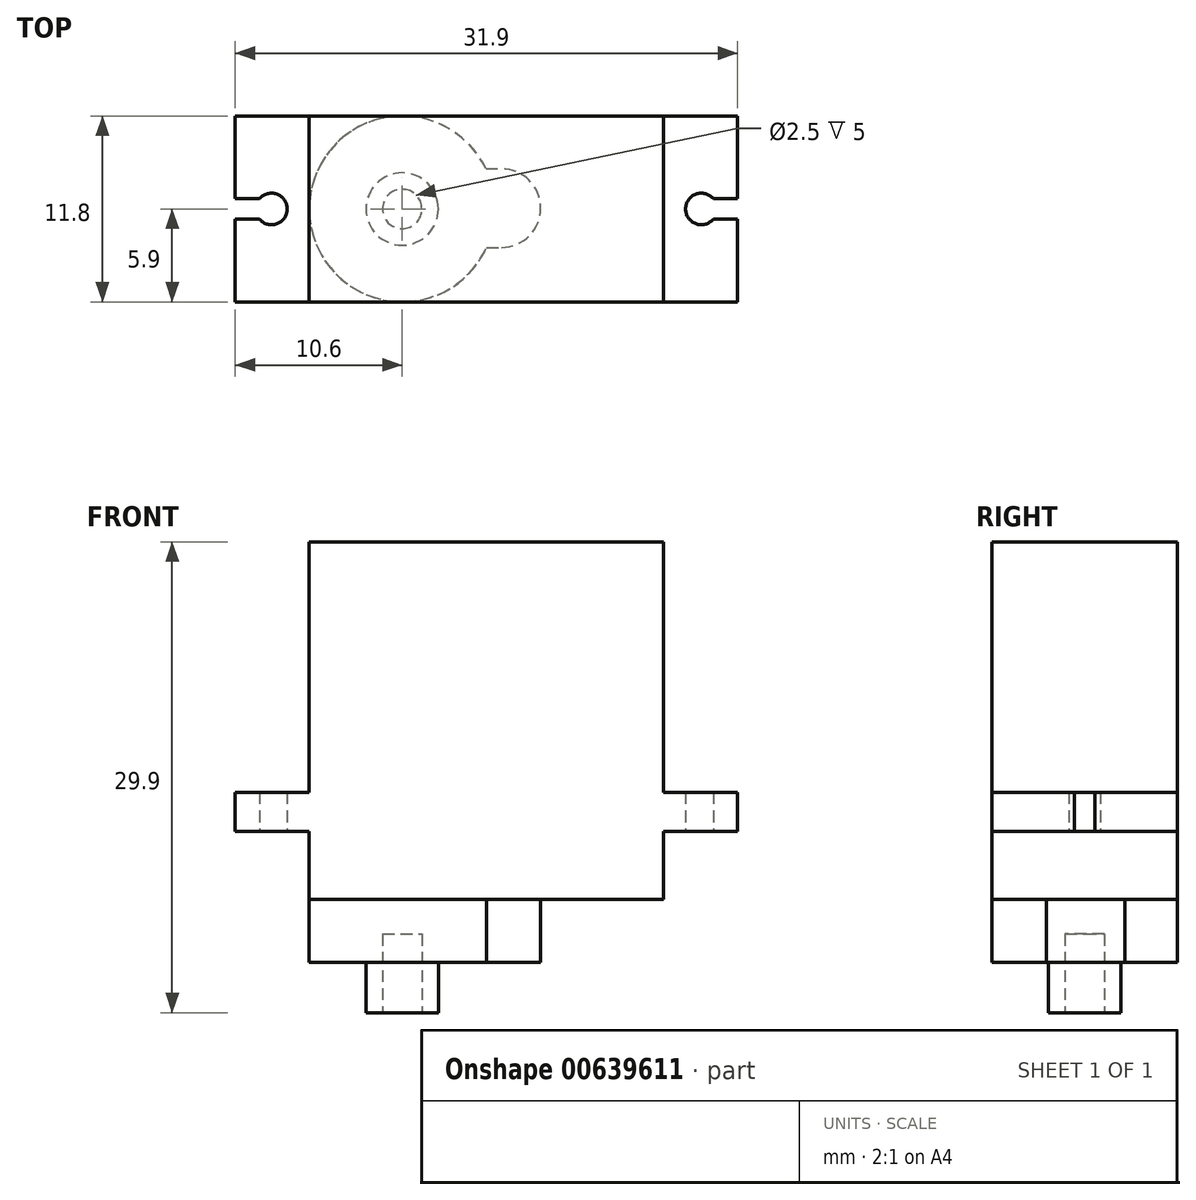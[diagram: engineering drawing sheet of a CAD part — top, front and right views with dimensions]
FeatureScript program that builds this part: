
annotation { "Feature Type Name" : "Feature", "Feature Type Description" : "" }
export const myFeature = defineFeature(function(context is Context, id is Id, definition is map)
    precondition{}
    {
        {
            var Q0;
            Q0=qCreatedBy(makeId("Top.planeOp"),FACE);
            var sketch = newSketch(context, id + "F0", { "sketchPlane" : qUnion([Q0])});
            skLineSegment(sketch, "E0.bottom", {"start": v(0, 0) * mm, "end": v(15.95, 0) * mm});
            skLineSegment(sketch, "E0.top", {"start": v(0, 11.8) * mm, "end": v(15.95, 11.8) * mm});
            skLineSegment(sketch, "E0.left", {"start": v(0, 0) * mm, "end": v(0, 11.8) * mm});
            skLineSegment(sketch, "E0.right", {"start": v(15.95, 0) * mm, "end": v(15.95, 11.8) * mm});
            skSolve(sketch);
        }
        {
            var Q0;
            Q0=makeQuery(id+"F0.imprint","IMPRINT",FACE,{"disambiguationData":[TD([[makeQuery(id+"F0.imprint","IMPRINT",EDGE,{"derivedFrom":sQuery(id+"F0.wireOp",EDGE,"E0.bottom")}),1.0]])]});
            var sketch = newSketch(context, id + "F1", { "sketchPlane" : qUnion([Q0])});
            skArc(sketch, "E1", {"start": v(1.54, 5.25) * mm, "mid": v(3.3, 5.9) * mm, "end": v(1.54, 6.55) * mm});
            skLineSegment(sketch, "E2", {"start": v(0, 5.25) * mm, "end": v(1.54, 5.25) * mm});
            skLineSegment(sketch, "E3", {"start": v(0, 6.55) * mm, "end": v(1.54, 6.55) * mm});
            skSolve(sketch);
        }
        {
            var Q0;
            Q0=makeQuery(id+"F1.imprint","IMPRINT",FACE,{"disambiguationData":[TD([[makeQuery(id+"F1.imprint","IMPRINT",EDGE,{"derivedFrom":sQuery(id+"F1.wireOp",EDGE,"E1")}),-1.0]])]});
            extrude(context, id + "F2", {"entities" : qUnion([Q0]), "depth" : 22.7 * mm, "offsetDistance" : 25 * mm});
        }
        {
            var Q0;
            Q0=makeQuery(id+"F2.opExtrude","SWEPT_FACE",FACE,{"disambiguationData":[OSD([sQuery(id+"F0.wireOp",EDGE,"E0.top")])]});
            var sketch = newSketch(context, id + "F3", { "sketchPlane" : qUnion([Q0])});
            skLineSegment(sketch, "E4", {"start": v(-4.7, 0) * mm, "end": v(-4.7, 4.3) * mm});
            skLineSegment(sketch, "E5", {"start": v(-4.7, 4.3) * mm, "end": v(0, 4.3) * mm});
            skLineSegment(sketch, "E6", {"start": v(0, 6.8) * mm, "end": v(-4.7, 6.8) * mm});
            skLineSegment(sketch, "E7", {"start": v(-4.7, 6.8) * mm, "end": v(-4.7, 22.7) * mm});
            skSolve(sketch);
        }
        {
            var Q0;
            {var subQ0=sQuery(id+"F3.wireOp",EDGE,"E4");Q0=makeQuery(id+"F3.imprint","IMPRINT",FACE,{"disambiguationData":[TD([[makeQuery(id+"F3.imprint","IMPRINT",EDGE,{"derivedFrom":subQ0}),-1.0]])]});}
            var Q1;
            {var subQ0=sQuery(id+"F3.wireOp",EDGE,"E6");Q1=makeQuery(id+"F3.imprint","IMPRINT",FACE,{"disambiguationData":[TD([[makeQuery(id+"F3.imprint","IMPRINT",EDGE,{"derivedFrom":subQ0}),-1.0]])]});}
            extrude(context, id + "F4", {"entities" : qUnion([Q0, Q1]), "operationType" : NewBodyOperationType.REMOVE, "endBound" : BoundingType.THROUGH_ALL, "oppositeDirection" : true, "depth" : 25 * mm, "offsetDistance" : 25 * mm});
        }
        {
            var Q0;
            Q0=makeQuery(id+"F2.opExtrude","SWEPT_BODY",BODY,{"disambiguationData":[OSD([sQuery(id+"F0.wireOp",EDGE,"E0.bottom"),sQuery(id+"F0.wireOp",EDGE,"E0.top"),sQuery(id+"F0.wireOp",EDGE,"E0.left"),sQuery(id+"F0.wireOp",EDGE,"E0.right")])]});
            var Q1;
            Q1=makeQuery(id+"F2.opExtrude","SWEPT_FACE",FACE,{"disambiguationData":[OSD([sQuery(id+"F0.wireOp",EDGE,"E0.right")])]});
            mirror(context, id + "F5", {"operationType" : NewBodyOperationType.ADD, "entities" : qUnion([Q0]), "mirrorPlane" : qUnion([Q1])});
        }
        {
            var Q0;
            {var subQ0=makeQuery(id+"F2.opExtrude","CAP_FACE",FACE,{"disambiguationData":[OSD([sQuery(id+"F0.wireOp",EDGE,"E0.bottom"),sQuery(id+"F0.wireOp",EDGE,"E0.top"),sQuery(id+"F0.wireOp",EDGE,"E0.left"),sQuery(id+"F0.wireOp",EDGE,"E0.right"),sQuery(id+"F1.wireOp",EDGE,"E1"),sQuery(id+"F1.wireOp",EDGE,"E2"),sQuery(id+"F1.wireOp",EDGE,"E3")])],"isStart":true});Q0=makeQuery(id+"F5.boolean.opBoolean","MERGE",FACE,{"derivedFrom":[subQ0,makeQuery(id+"F5.opPattern","COPY",FACE,{"derivedFrom":subQ0,"instanceName":"1"})]});}
            var sketch = newSketch(context, id + "F6", { "sketchPlane" : qUnion([Q0])});
            skArc(sketch, "E8", {"start": v(15.97, -3.46) * mm, "mid": v(4.7, -5.84) * mm, "end": v(15.92, -8.46) * mm});
            skArc(sketch, "E9", {"start": v(16.9, -8.46) * mm, "mid": v(19.4, -5.96) * mm, "end": v(16.9, -3.46) * mm});
            skLineSegment(sketch, "E10", {"start": v(15.97, -3.46) * mm, "end": v(16.9, -3.46) * mm});
            skLineSegment(sketch, "E11", {"start": v(15.92, -8.46) * mm, "end": v(16.9, -8.46) * mm});
            skCircle(sketch, "E12", {"center": v(10.6, -5.9) * mm, "radius": 2.3 * mm});
            skSolve(sketch);
        }
        {
            var Q0;
            Q0=makeQuery(id+"F6.imprint","IMPRINT",FACE,{"disambiguationData":[TD([[makeQuery(id+"F6.imprint","IMPRINT",EDGE,{"derivedFrom":sQuery(id+"F6.wireOp",EDGE,"E9")}),1.0]])]});
            extrude(context, id + "F7", {"entities" : qUnion([Q0]), "operationType" : NewBodyOperationType.ADD, "depth" : 4 * mm, "offsetDistance" : 25 * mm});
        }
        {
            var Q0;
            Q0=makeQuery(id+"F6.imprint","IMPRINT",FACE,{"disambiguationData":[TD([[makeQuery(id+"F6.imprint","IMPRINT",EDGE,{"derivedFrom":sQuery(id+"F6.wireOp",EDGE,"E12")}),1.0]])]});
            extrude(context, id + "F8", {"entities" : qUnion([Q0]), "operationType" : NewBodyOperationType.ADD, "depth" : 7.2 * mm, "offsetDistance" : 25 * mm});
        }
        {
            var Q0;
            Q0=makeQuery(id+"F8.opExtrude","CAP_FACE",FACE,{"disambiguationData":[OSD([sQuery(id+"F6.wireOp",EDGE,"E12")])],"isStart":false});
            var sketch = newSketch(context, id + "F9", { "sketchPlane" : qUnion([Q0])});
            skCircle(sketch, "E13", {"center": v(10.6, -5.9) * mm, "radius": 1.25 * mm});
            skSolve(sketch);
        }
        {
            var Q0;
            Q0=makeQuery(id+"F9.imprint","IMPRINT",FACE,{"disambiguationData":[TD([[makeQuery(id+"F9.imprint","IMPRINT",EDGE,{"derivedFrom":sQuery(id+"F9.wireOp",EDGE,"E13")}),1.0]])]});
            extrude(context, id + "F10", {"entities" : qUnion([Q0]), "operationType" : NewBodyOperationType.REMOVE, "oppositeDirection" : true, "depth" : 5 * mm, "offsetDistance" : 25 * mm});
        }
    });
